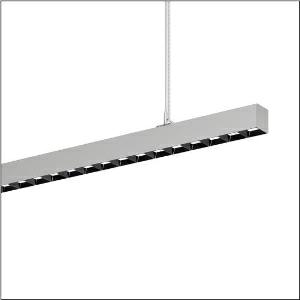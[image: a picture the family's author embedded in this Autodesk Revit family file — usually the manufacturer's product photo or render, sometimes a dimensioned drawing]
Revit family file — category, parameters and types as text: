
# Revit family: silica_r__21_51mx31tctds_9889
name_source: partatom
category: Lighting Fixtures
units: mm (PartAtom-declared; Revit-internal decimal feet)

## family parameters
Cut with Voids When Loaded = No
Host = Face
Light Source = No
Part Type = Normal
Room Calculation Point = No
Round Connector Dimension = Use Diameter
Shared = No

## types (1)
- --- (1 x LED, 15550 lm, 133.9 W, 6500K)
    Apparent Load = 134 VA
    CIE Flux Codes = 85 99 100 60 100
    Color Rendering = 80
    Color Temperature = 6500K
    Default Elevation = 1800 mm
    Description = Silica® 21, office luminaire, primary light control with darklight reflector, of PMMA, black, CAT 2 (L<= 3000cd/m²), light emission: direct/indirect distribution, primary light characteristic: symmetric, installation type: suspended mounting, LED, rated luminous flux: 15.550lm, luminous efficacy: 111lm/W, light colour: 8tw, colour temperature: 2700..6500K, control gear: ECG DALI, with terminal, 3+2-pole, max. 2.5mm², mains connection: 220..240V, AC, 50/60Hz, rated input power: 140.6W, luminaire housing, of aluminium, metallic grey (RAL 9006), length: 3.004mm, width: 53mm, height: 53mm, protection rating (complete): IP20, insulation class (complete): insulation class I (protective earthing), certification: CE, permissible operating ambient temperature: 0..+35°C, standard: EN 50419, packaging unit: 1 piece
    Height = 53 mm
    Lamp = 1 x LED
    Lamp Light Flux = 15550 lm
    Lamp Power = 133.9 W
    Lamp count = 1
    Length = 3004 mm
    Luminous efficacy = 116 lm/W
    Manufacturer = Siteco
    ModVariant = No
    Model = 51MX31TCTDS
    Mounting Place = Ceiling
    Mounting Type = Pendant
    Number of Poles = 1
    OnlyDefault = Yes
    Power Factor = 1
    Product Name = Silica® 21
    Product group = office luminaire | ceiling pendant
    ProductGroupID = 902
    Protection Class = Protection class I
    Protection Degree = IP 20
    RLX_Detail_Level = 1
    RLX_Emergency_Light_Flux = 0 lm
    RLX_Emergency_Type = 0
    RLX_Emergency_Type_DB = No
    RlxData = <blob elided: 62357 chars, md5=12817eb4>
    Socket = socket
    Standby Power = 0 W
    System Light Flux = 15550 lm
    System Power = 134 W
    Type Comments = individual setting
    Type Image = l_1313642.jpg
    URL = http://relux.com
    VarID = @adj_089229
    Voltage = 0 V
    Weight = 0.00 kg
    Width = 53 mm

## geometry (parser evidence)
native form markers: Blend x4, Sweep x11
no freeform markers — native parametric forms only
